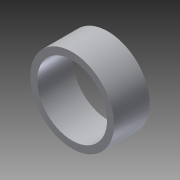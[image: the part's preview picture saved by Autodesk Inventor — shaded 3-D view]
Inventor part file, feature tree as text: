
AUTODESK INVENTOR PART (.ipt)
format: ipt  version: 2014 (Build 180170000, 170)  size: 87,552 bytes
history: native  units: in
note: dims shown in document units (in); Inventor stores cm internally (conversion verified against a paired STEP export)
features: extrude x1
ambient origin geometry x8: Origin, YZ Plane, XZ Plane, XY Plane, X Axis, Y Axis, Z Axis, Center Point
bodies: Solid1 (feature_tree)
feature tree (1):
  extrude  "Extrusion1"  Depth=0.625in
